# Revit family: Detail_Batten_Knotwood_50mmSuite
name_source: partatom
category: Detail Items
units: mm (PartAtom-declared; Revit-internal decimal feet)

## family parameters
Rotate with component = No
Section Shape = Not Defined
Shared = No

## types (8) — shared parameters
Manufacturer = Knotwood
ManufacturerOverallWidth = 50 mm  [stored 0.164042 ft]
ManufacturerURLProductSpecific = https://www.knotwood.com.au
ModifiedIssue = 20231130 $
URL = https://www.knotwood.com.au

## per-type parameters (varying)
| type | Description | FemaleType | ManufacturerOverallDepth | ManufacturerSpecCode | Model |
| 200mm (KEB20050F/SF) | Knotwood 50mm Batten Suite (KEB20050F/SF) | z_DetailItem_Batten_Knotwood_50mmSuite_Female : 200mm x 50mm (KEB20050F-SF) | 200 mm  [stored 0.656168 ft] | KEB20050F/SF | KEB20050F/SF |
| 50mm (KEB5050F/SF) | Knotwood 50mm Batten Suite (KEB5050F/SF) | z_DetailItem_Batten_Knotwood_50mmSuite_Female : 50mm x 50mm (KEB5050F/SF) | 50 mm  [stored 0.164042 ft] | KEB5050F/SF | KEB5050F/SF |
| 100mm (KEB10050F/SF) | Knotwood 50mm Batten Suite (KEB10050F/SF) | z_DetailItem_Batten_Knotwood_50mmSuite_Female : 100mm x 50mm (KEB10050F-SF) | 100 mm  [stored 0.328084 ft] | KEB10050F/SF | KEB10050F/SF |
| 150mm (KEB15050F/SF) | Knotwood 50mm Batten Suite (KEB15050F/SF) | z_DetailItem_Batten_Knotwood_50mmSuite_Female : 150mm x 50mm (KEB15050F-SF) | 150 mm | KEB15050F/SF | KEB15050F/SF |
| Angle 80mm (KEB8050AF) | Knotwood 50mm Batten Suite (KEB8050AF) | z_DetailItem_Batten_Knotwood_50mmSuite_Female : 50mm x 50mm Angle (KEBF5050A) | 80 mm  [stored 0.262467 ft] | KEB8050AF | KEB8050AF |
| Dome 54mm (KEB5450DF) | Knotwood 50mm Batten Suite (KEB5450DF) | z_DetailItem_Batten_Knotwood_50mmSuite_Female : 50mm x 50mm Dome (KEB5450DF) | 54 mm  [stored 0.177165 ft] | KEB5450DF | KEB5450DF |
| Seam 150mm (KEB15050FE) | Knotwood 50mm Batten Suite (KEB15050FE) | z_DetailItem_Batten_Knotwood_50mmSuite_Seam_Female : 150mm x 50mm (KEB15050FE) | 150 mm | KEB15050FE | KEB15050FE |
| Seam 200mm (KEB20050FE) | Knotwood 50mm Batten Suite (KEB20050FE) | z_DetailItem_Batten_Knotwood_50mmSuite_Seam_Female : 200mm x 50mm (KEB20050FE) | 200 mm  [stored 0.656168 ft] | KEB20050FE | KEB20050FE |

note: [stored X ft] marks values corroborated as IEEE doubles in the binary element streams (Revit-internal decimal feet)

## geometry (parser evidence)
native form markers: Sweep x2
no freeform markers — native parametric forms only
